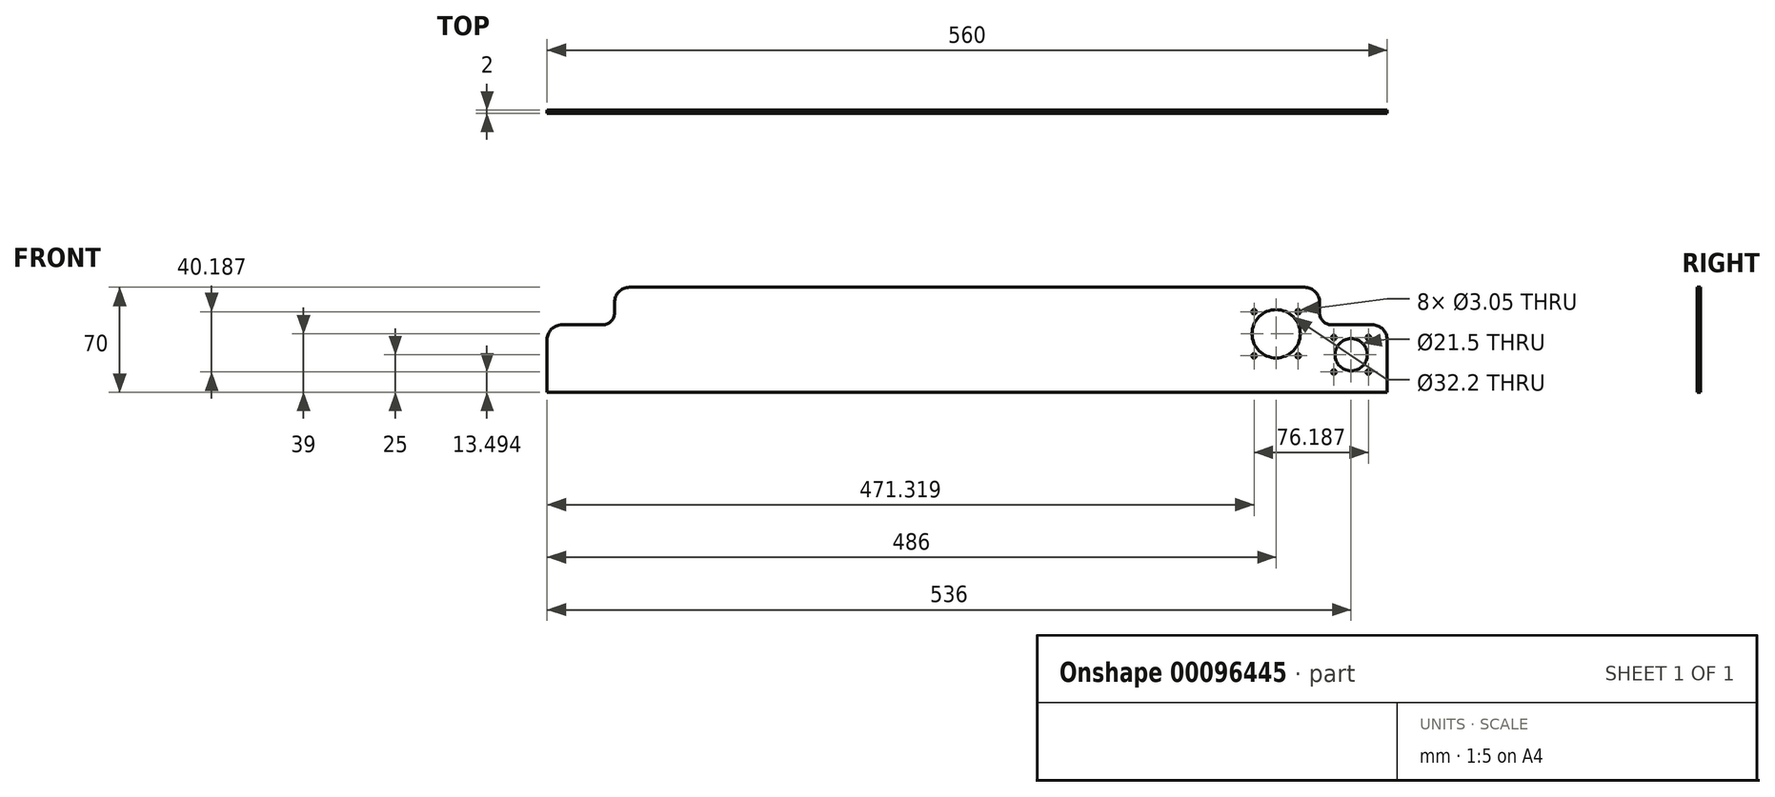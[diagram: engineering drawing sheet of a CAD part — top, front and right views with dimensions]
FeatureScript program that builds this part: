
annotation { "Feature Type Name" : "Feature", "Feature Type Description" : "" }
export const myFeature = defineFeature(function(context is Context, id is Id, definition is map)
    precondition{}
    {
        {
            var Q0;
            Q0=qCreatedBy(makeId("Front.planeOp"),FACE);
            var sketch = newSketch(context, id + "F0", { "sketchPlane" : qUnion([Q0])});
            skLineSegment(sketch, "E0", {"start": v(0, 0) * mm, "end": v(280, 0) * mm});
            skLineSegment(sketch, "E1", {"start": v(280, 0) * mm, "end": v(280, 35) * mm});
            skLineSegment(sketch, "E2", {"start": v(270, 45) * mm, "end": v(243, 45) * mm});
            skLineSegment(sketch, "E3", {"start": v(235, 53) * mm, "end": v(235, 60) * mm});
            skCircle(sketch, "E4", {"center": v(256, 25) * mm, "radius": 10.75 * mm});
            skCircle(sketch, "E5", {"center": v(267.5, 36.5) * mm, "radius": 1.52 * mm});
            skCircle(sketch, "E6", {"center": v(206, 39) * mm, "radius": 16.1 * mm});
            skCircle(sketch, "E7", {"center": v(220.68, 53.68) * mm, "radius": 1.52 * mm});
            skLineSegment(sketch, "E8", {"start": v(252.24, 25) * mm, "end": v(256, 25) * mm, "construction": true});
            skLineSegment(sketch, "E9", {"start": v(256, 25) * mm, "end": v(256, 41.26) * mm, "construction": true});
            skLineSegment(sketch, "E10", {"start": v(193.83, 39) * mm, "end": v(206, 39) * mm, "construction": true});
            skLineSegment(sketch, "E11", {"start": v(206, 39) * mm, "end": v(206, 40.35) * mm, "construction": true});
            skCircle(sketch, "E12.MirrorC", {"center": v(191.32, 53.68) * mm, "radius": 1.52 * mm});
            skCircle(sketch, "E13.MirrorC", {"center": v(220.68, 24.32) * mm, "radius": 1.52 * mm});
            skCircle(sketch, "E14.MirrorC", {"center": v(191.32, 24.32) * mm, "radius": 1.52 * mm});
            skCircle(sketch, "E15.MirrorC", {"center": v(244.5, 36.5) * mm, "radius": 1.52 * mm});
            skCircle(sketch, "E16.MirrorC", {"center": v(267.5, 13.5) * mm, "radius": 1.52 * mm});
            skCircle(sketch, "E17.MirrorC", {"center": v(244.5, 13.5) * mm, "radius": 1.52 * mm});
            skPoint(sketch, "E18.visualSharp", {"position": v(235, 45) * mm});
            skArc(sketch, "E18.filletArc", {"start": v(235, 53) * mm, "mid": v(237.34, 47.34) * mm, "end": v(243, 45) * mm});
            skPoint(sketch, "E19.visualSharp", {"position": v(280, 45) * mm});
            skArc(sketch, "E19.filletArc", {"start": v(280, 35) * mm, "mid": v(277.07, 42.07) * mm, "end": v(270, 45) * mm});
            skLineSegment(sketch, "E20", {"start": v(0, 70) * mm, "end": v(225, 70) * mm});
            skArc(sketch, "E21.filletArc", {"start": v(235, 60) * mm, "mid": v(232.07, 67.07) * mm, "end": v(225, 70) * mm});
            skLineSegment(sketch, "E22.MirrorCS", {"start": v(0, 0) * mm, "end": v(-280, 0) * mm});
            skLineSegment(sketch, "E23.MirrorCS", {"start": v(-280, 0) * mm, "end": v(-280, 35) * mm});
            skArc(sketch, "E24.MirrorCS", {"start": v(-280, 35) * mm, "mid": v(-277.07, 42.07) * mm, "end": v(-270, 45) * mm});
            skLineSegment(sketch, "E25.MirrorCS", {"start": v(-270, 45) * mm, "end": v(-243, 45) * mm});
            skArc(sketch, "E26.MirrorCS", {"start": v(-235, 53) * mm, "mid": v(-237.34, 47.34) * mm, "end": v(-243, 45) * mm});
            skLineSegment(sketch, "E27.MirrorCS", {"start": v(0, 70) * mm, "end": v(-225, 70) * mm});
            skLineSegment(sketch, "E28.MirrorCS", {"start": v(-235, 53) * mm, "end": v(-235, 60) * mm});
            skArc(sketch, "E29.MirrorCS", {"start": v(-235, 60) * mm, "mid": v(-232.07, 67.07) * mm, "end": v(-225, 70) * mm});
            skSolve(sketch);
        }
        {
            var Q0;
            Q0 = qSketchRegion(id + "F0", true);
            extrude(context, id + "F1", {"entities" : qUnion([Q0]), "depth" : 2 * mm});
        }
    });
